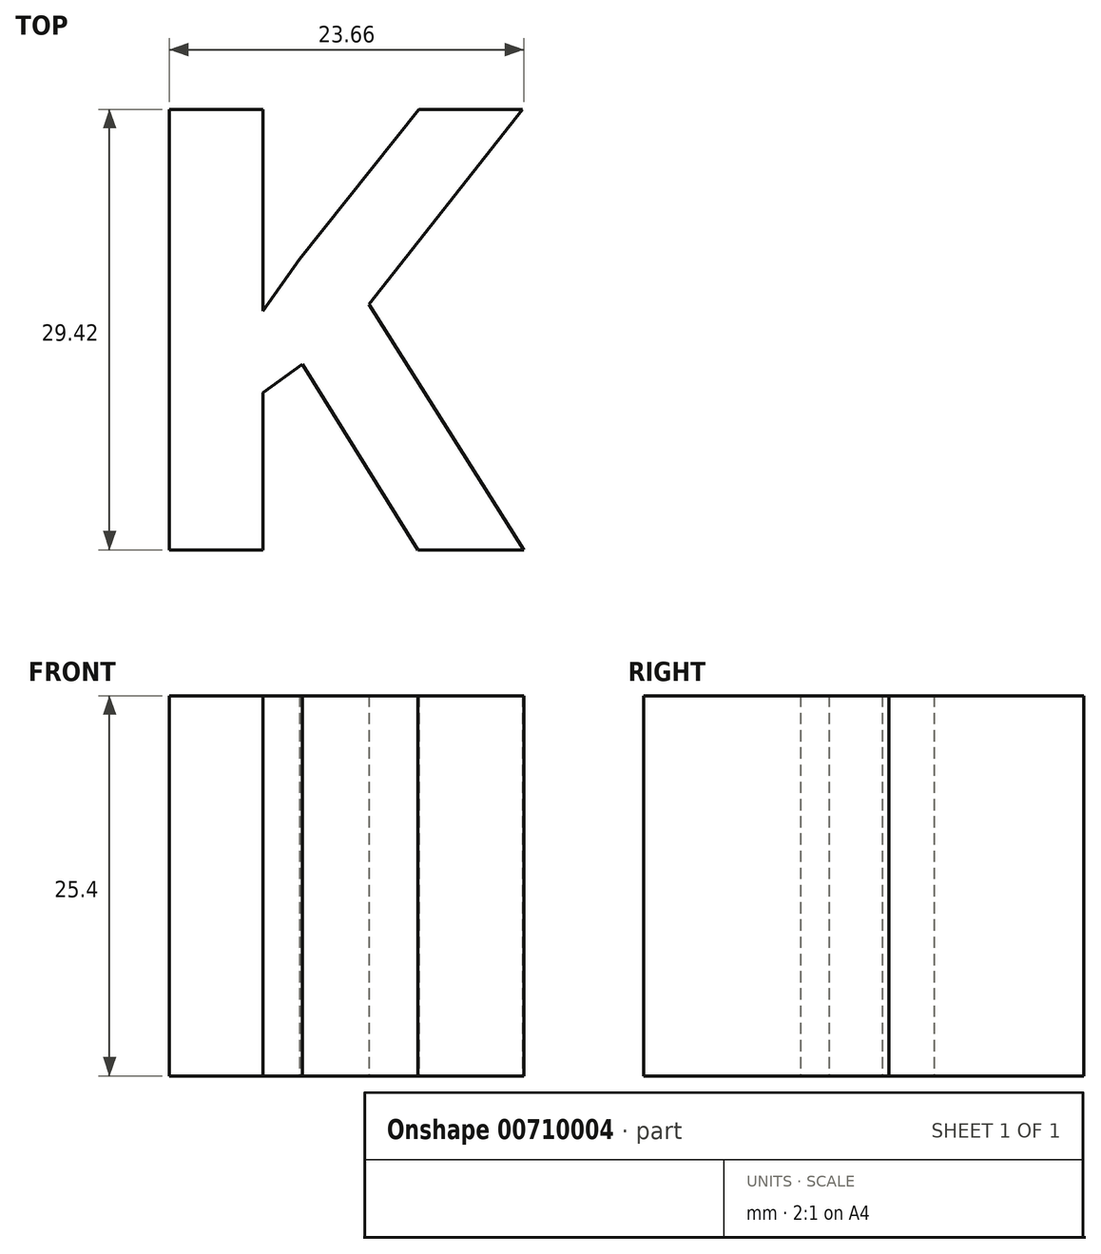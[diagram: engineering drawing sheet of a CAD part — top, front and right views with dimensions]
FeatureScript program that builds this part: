
annotation { "Feature Type Name" : "Feature", "Feature Type Description" : "" }
export const myFeature = defineFeature(function(context is Context, id is Id, definition is map)
    precondition{}
    {
        {
            var Q0;
            Q0=qCreatedBy(makeId("Top.planeOp"),FACE);
            cPlane(context, id + "F0", {"entities" : qUnion([Q0]), "cplaneType" : CPlaneType.OFFSET, "offset" : 25.4 * mm, "width" : 152.4 * mm, "height" : 152.4 * mm});
        }
        {
            var Q0;
            Q0=qCreatedBy(id+"F0.planeOp",FACE);
            var sketch = newSketch(context, id + "F1", { "sketchPlane" : qUnion([Q0])});
            skText(sketch, "E0", { "text": "K", "fontName": "OpenSans-Bold.ttf"});
            const initialGuessF1  = {"E0": [-0.01933, 0, 1, 0, 0.02967]};
            skSetInitialGuess(sketch, initialGuessF1);
            skSolve(sketch);
        }
        {
            var Q0;
            Q0=makeQuery(id+"F1.imprint","IMPRINT",FACE,{"disambiguationData":[TD([[makeQuery(id+"F1.imprint","IMPRINT",EDGE,{"derivedFrom":sQuery(id+"F1.wireOp",EDGE,"E0.sketch_text.stroke-0")}),-1.0]])]});
            extrude(context, id + "F2", {"entities" : qUnion([Q0]), "depth" : 25.4 * mm, "offsetDistance" : 25.4 * mm});
        }
    });
